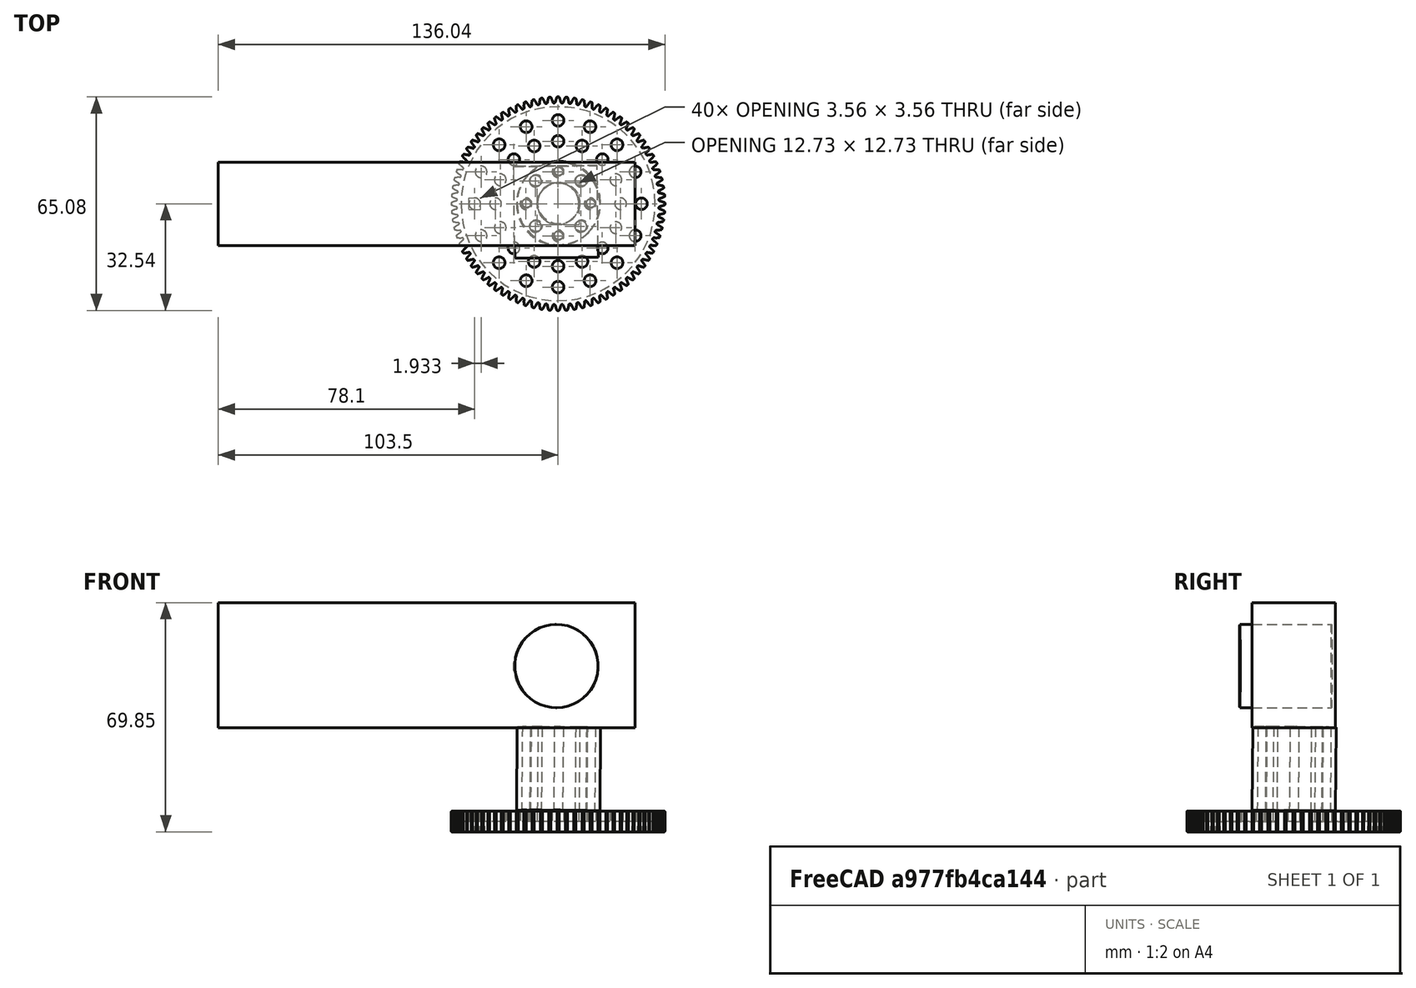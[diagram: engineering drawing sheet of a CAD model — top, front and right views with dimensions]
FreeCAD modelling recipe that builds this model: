
FCSTD DOCUMENT  (FreeCAD 0.15R4671 (Git))
Label: tubemount
License: All rights reserved
LicenseURL: http://en.wikipedia.org/wiki/All_rights_reserved
objects: Part::Feature×2, Part::Box×1, Part::Cylinder×1
note: 4 computed .brp shape members not serialized (recipe doc carries the construction recipe); baked Part::Feature solids carry a one-line shape summary decoded from their .brp

FEATURE [Part::Feature] Part__Feature  label="615206"
  Placement = pos=(0,0,3.175) rot=(0,-1,0;1.5708rad)
  shape: bbox 65.09 x 65.09 x 6.35 mm, 760 faces (baked)
FEATURE [Part::Feature] Part__Feature001  label="545386"
  Placement = pos=(0.0263083,-5.32278e-06,6.532) rot=(-0.730992,0.68238,-0.002886;0.01157rad)
  shape: bbox 25.59 x 25.61 x 25.69 mm, 22 faces (baked)
FEATURE [Part::Box] Box  label="Cube"
  Height = 38.1
  Length = 127
  Placement = pos=(-103.505,-12.7,31.75) rot=(0,0,1;0rad)
  Width = 25.4
FEATURE [Part::Cylinder] Cylinder
  Angle = 360
  Height = 27.94
  Placement = pos=(-0.483033,-16.4367,50.513) rot=(0.582648,-0.571473,-0.577876;4.18705rad)
  Radius = 12.7
